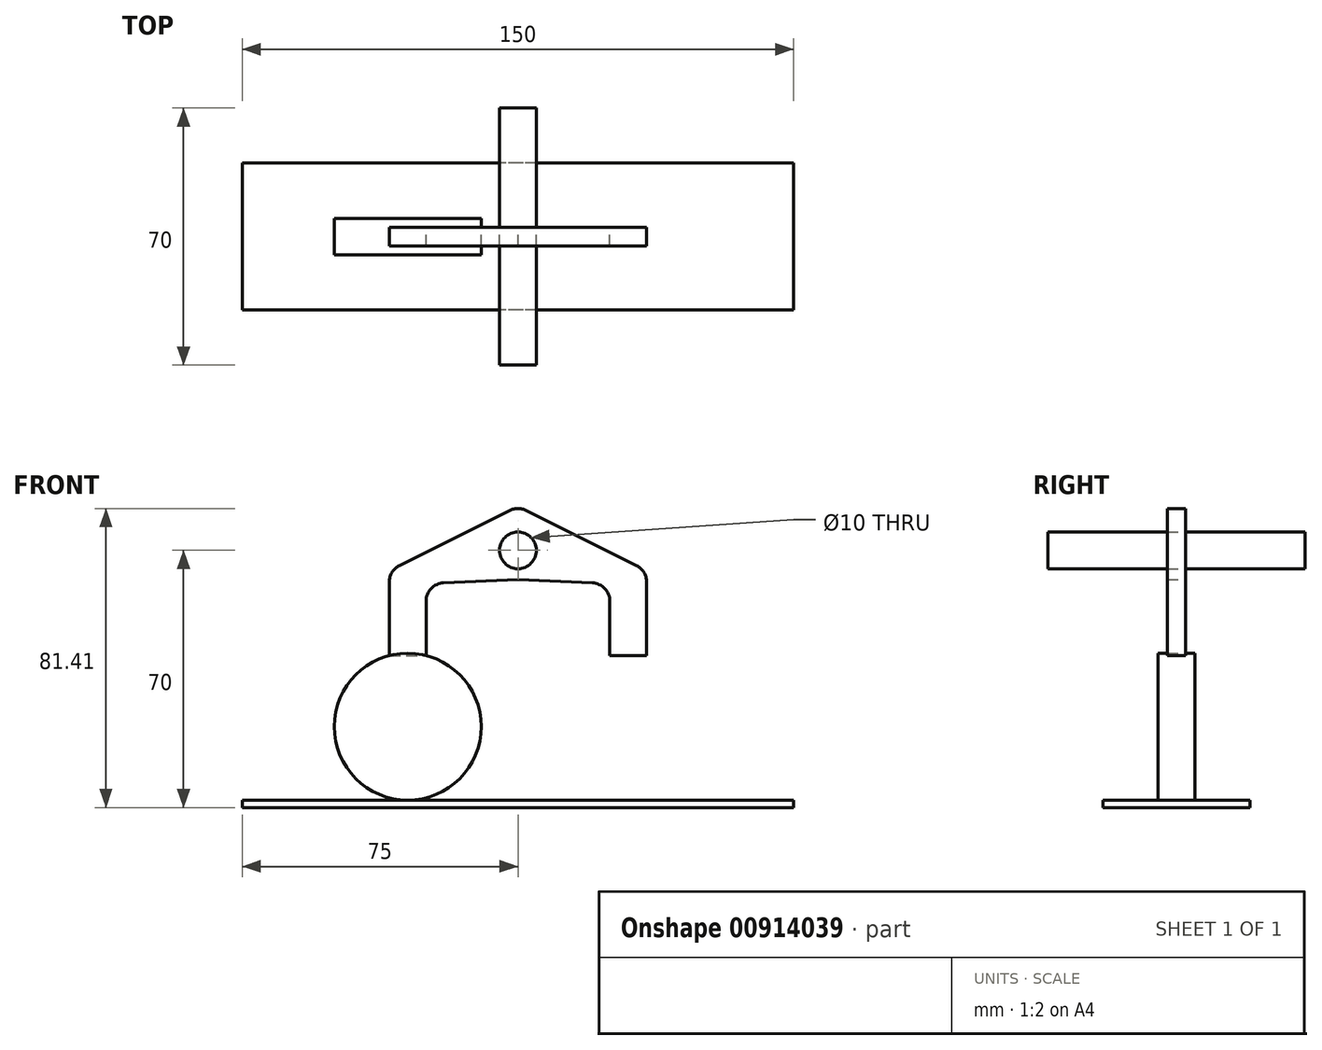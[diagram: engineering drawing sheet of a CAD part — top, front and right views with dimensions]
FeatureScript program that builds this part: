
annotation { "Feature Type Name" : "Feature", "Feature Type Description" : "" }
export const myFeature = defineFeature(function(context is Context, id is Id, definition is map)
    precondition{}
    {
        {
            var Q0;
            Q0=qCreatedBy(makeId("Front.planeOp"),FACE);
            var sketch = newSketch(context, id + "F0", { "sketchPlane" : qUnion([Q0])});
            skLineSegment(sketch, "E0", {"start": v(0, 0) * mm, "end": v(-60, 0) * mm, "construction": true});
            skCircle(sketch, "E1", {"center": v(-30, 0) * mm, "radius": 20 * mm});
            skCircle(sketch, "E2.MirrorC", {"center": v(30, 0) * mm, "radius": 20 * mm});
            skSolve(sketch);
        }
        {
            var Q0;
            Q0=makeQuery(id+"F0.imprint","IMPRINT",FACE,{"disambiguationData":[TD([[makeQuery(id+"F0.imprint","IMPRINT",EDGE,{"derivedFrom":sQuery(id+"F0.wireOp",EDGE,"E1")}),1.0]])]});
            var Q1;
            Q1=makeQuery(id+"F0.imprint","IMPRINT",FACE,{"disambiguationData":[TD([[makeQuery(id+"F0.imprint","IMPRINT",EDGE,{"derivedFrom":sQuery(id+"F0.wireOp",EDGE,"E2.MirrorC")}),-1.0]])]});
            extrude(context, id + "F1", {"entities" : qUnion([Q0, Q1]), "endBound" : BoundingType.SYMMETRIC, "depth" : 10 * mm, "offsetDistance" : 25 * mm});
        }
        {
            var Q0;
            Q0=qCreatedBy(makeId("Front.planeOp"),FACE);
            var sketch = newSketch(context, id + "F2", { "sketchPlane" : qUnion([Q0])});
            skLineSegment(sketch, "E3", {"start": v(0, 60) * mm, "end": v(-35, 42.5) * mm});
            skLineSegment(sketch, "E4", {"start": v(-35, 42.5) * mm, "end": v(-35, 19.36) * mm});
            skLineSegment(sketch, "E5.MirrorCS", {"start": v(0, 60) * mm, "end": v(35, 42.5) * mm});
            skLineSegment(sketch, "E6.MirrorCS", {"start": v(35, 42.5) * mm, "end": v(35, 19.36) * mm});
            skLineSegment(sketch, "E7", {"start": v(0, 40) * mm, "end": v(-25, 38.95) * mm});
            skLineSegment(sketch, "E8", {"start": v(-25, 38.95) * mm, "end": v(-25, 19.36) * mm});
            skLineSegment(sketch, "E9.MirrorCS", {"start": v(0, 40) * mm, "end": v(25, 38.95) * mm});
            skLineSegment(sketch, "E10.MirrorCS", {"start": v(25, 38.95) * mm, "end": v(25, 19.36) * mm});
            skLineSegment(sketch, "E11", {"start": v(-35, 19.36) * mm, "end": v(-25, 19.36) * mm});
            skLineSegment(sketch, "E12", {"start": v(25, 19.36) * mm, "end": v(35, 19.36) * mm});
            skSolve(sketch);
        }
        {
            var Q0;
            Q0=makeQuery(id+"F2.imprint","IMPRINT",FACE,{"disambiguationData":[TD([[makeQuery(id+"F2.imprint","IMPRINT",EDGE,{"derivedFrom":sQuery(id+"F2.wireOp",EDGE,"E3")}),1.0]])]});
            extrude(context, id + "F3", {"entities" : qUnion([Q0]), "endBound" : BoundingType.SYMMETRIC, "depth" : 5 * mm, "offsetDistance" : 25 * mm});
        }
        {
            var Q0;
            Q0=makeQuery(id+"F3.opExtrude","SWEPT_EDGE",EDGE,{"disambiguationData":[OSD([sQuery(id+"F2.wireOp",EDGE,"E3"),sQuery(id+"F2.wireOp",EDGE,"E5.MirrorCS")])]});
            var Q1;
            Q1=makeQuery(id+"F3.opExtrude","SWEPT_EDGE",EDGE,{"disambiguationData":[OSD([sQuery(id+"F2.wireOp",EDGE,"E3"),sQuery(id+"F2.wireOp",EDGE,"E4")])]});
            var Q2;
            Q2=makeQuery(id+"F3.opExtrude","SWEPT_EDGE",EDGE,{"disambiguationData":[OSD([sQuery(id+"F2.wireOp",EDGE,"E5.MirrorCS"),sQuery(id+"F2.wireOp",EDGE,"E6.MirrorCS")])]});
            var Q3;
            Q3=makeQuery(id+"F3.opExtrude","SWEPT_EDGE",EDGE,{"disambiguationData":[OSD([sQuery(id+"F2.wireOp",EDGE,"E7"),sQuery(id+"F2.wireOp",EDGE,"E8")])]});
            var Q4;
            Q4=makeQuery(id+"F3.opExtrude","SWEPT_EDGE",EDGE,{"disambiguationData":[OSD([sQuery(id+"F2.wireOp",EDGE,"E9.MirrorCS"),sQuery(id+"F2.wireOp",EDGE,"E10.MirrorCS")])]});
            fillet(context, id + "F4", {"entities" : qUnion([Q0, Q1, Q2, Q3, Q4]), "radius" : 5 * mm, "tangentPropagation" : true, "allowEdgeOverflow" : false});
        }
        {
            var Q0;
            Q0=qCreatedBy(makeId("Top.planeOp"),FACE);
            cPlane(context, id + "F5", {"entities" : qUnion([Q0]), "cplaneType" : CPlaneType.OFFSET, "offset" : 20 * mm, "oppositeDirection" : true, "width" : 150 * mm, "height" : 150 * mm});
        }
        {
            var Q0;
            Q0=qCreatedBy(id+"F5.planeOp",FACE);
            var sketch = newSketch(context, id + "F6", { "sketchPlane" : qUnion([Q0])});
            skLineSegment(sketch, "E13.bottom", {"start": v(75, -20) * mm, "end": v(-75, -20) * mm});
            skLineSegment(sketch, "E13.top", {"start": v(75, 20) * mm, "end": v(-75, 20) * mm});
            skLineSegment(sketch, "E13.left", {"start": v(75, -20) * mm, "end": v(75, 20) * mm});
            skLineSegment(sketch, "E13.right", {"start": v(-75, -20) * mm, "end": v(-75, 20) * mm});
            skPoint(sketch, "E13.middle", {"position": v(0, 0) * mm});
            skSolve(sketch);
        }
        {
            var Q0;
            Q0=makeQuery(id+"F6.imprint","IMPRINT",FACE,{"disambiguationData":[TD([[makeQuery(id+"F6.imprint","IMPRINT",EDGE,{"derivedFrom":sQuery(id+"F6.wireOp",EDGE,"E13.bottom")}),-1.0]])]});
            extrude(context, id + "F7", {"entities" : qUnion([Q0]), "oppositeDirection" : true, "depth" : 2 * mm, "offsetDistance" : 25 * mm});
        }
        {
            var Q0;
            Q0=qCreatedBy(makeId("Front.planeOp"),FACE);
            var sketch = newSketch(context, id + "F8", { "sketchPlane" : qUnion([Q0])});
            skCircle(sketch, "E14", {"center": v(0, 48) * mm, "radius": 5 * mm});
            skSolve(sketch);
        }
        {
            var Q0;
            Q0 = qSketchRegion(id + "F8", true);
            extrude(context, id + "F9", {"entities" : qUnion([Q0]), "operationType" : NewBodyOperationType.REMOVE, "endBound" : BoundingType.SYMMETRIC, "oppositeDirection" : true, "depth" : 5 * mm, "offsetDistance" : 25 * mm});
        }
        {
            var Q0;
            Q0 = qSketchRegion(id + "F8", true);
            extrude(context, id + "F10", {"entities" : qUnion([Q0]), "endBound" : BoundingType.SYMMETRIC, "depth" : 70 * mm, "offsetDistance" : 25 * mm});
        }
    });
